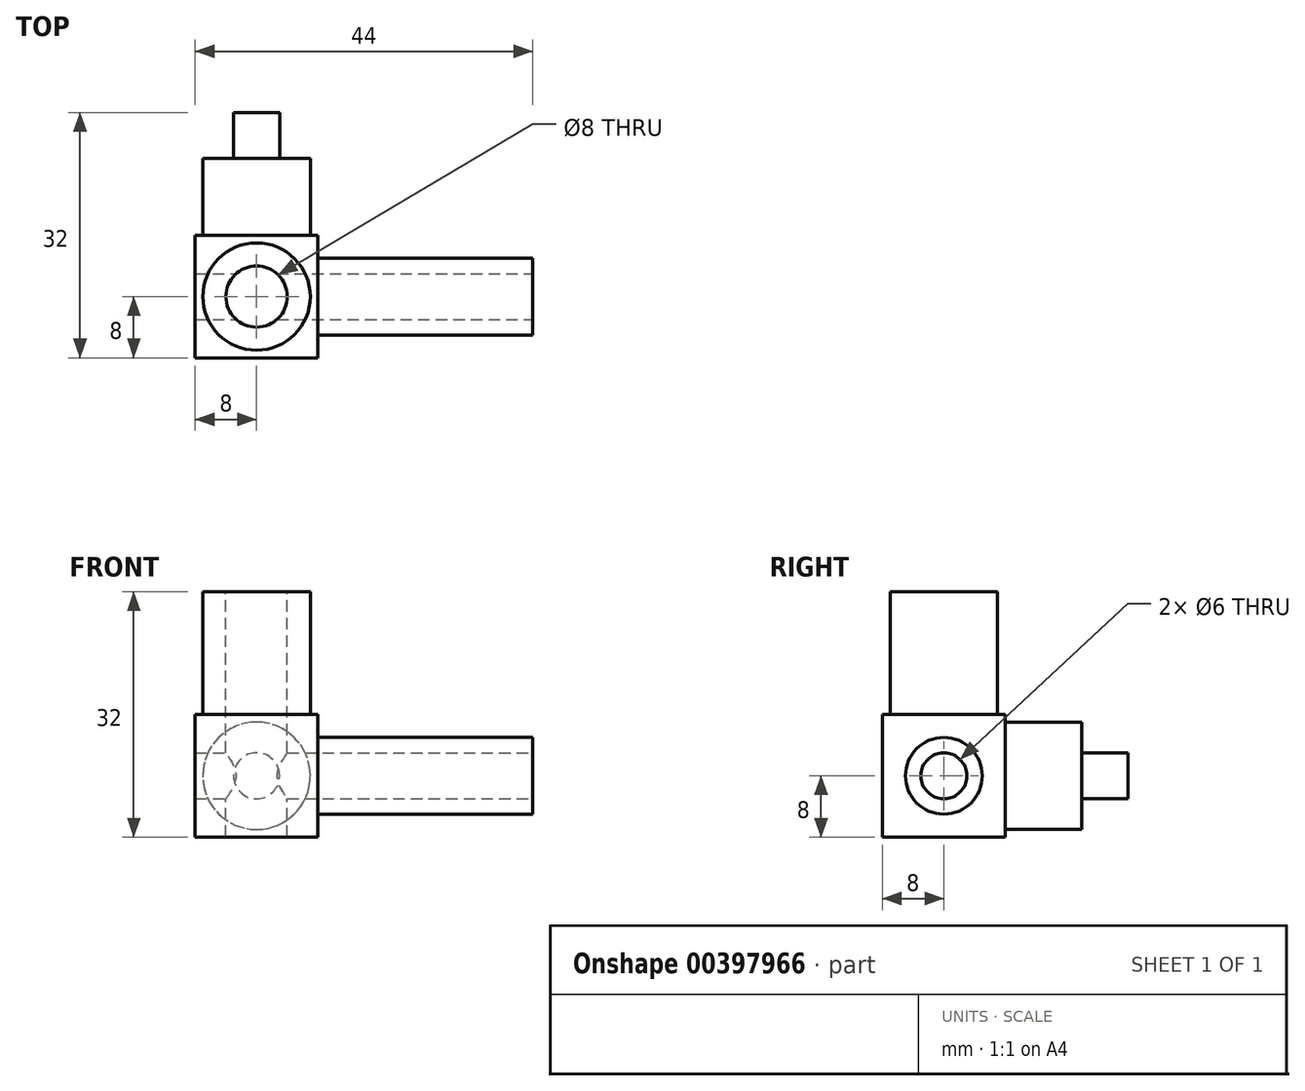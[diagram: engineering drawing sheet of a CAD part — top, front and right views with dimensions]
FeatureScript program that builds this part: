
annotation { "Feature Type Name" : "Feature", "Feature Type Description" : "" }
export const myFeature = defineFeature(function(context is Context, id is Id, definition is map)
    precondition{}
    {
        {
            var Q0;
            Q0=qCreatedBy(makeId("Right.planeOp"),FACE);
            var sketch = newSketch(context, id + "F0", { "sketchPlane" : qUnion([Q0])});
            skLineSegment(sketch, "E0.bottom", {"start": v(0, 0) * mm, "end": v(16, 0) * mm});
            skLineSegment(sketch, "E0.top", {"start": v(0, 16) * mm, "end": v(16, 16) * mm});
            skLineSegment(sketch, "E0.left", {"start": v(0, 0) * mm, "end": v(0, 16) * mm});
            skLineSegment(sketch, "E0.right", {"start": v(16, 0) * mm, "end": v(16, 16) * mm});
            skSolve(sketch);
        }
        {
            var Q0;
            Q0=makeQuery(id+"F0.imprint","IMPRINT",FACE,{"disambiguationData":[TD([[makeQuery(id+"F0.imprint","IMPRINT",EDGE,{"derivedFrom":sQuery(id+"F0.wireOp",EDGE,"E0.bottom")}),1.0]])]});
            extrude(context, id + "F1", {"entities" : qUnion([Q0]), "depth" : 16 * mm});
        }
        {
            var Q0;
            Q0=makeQuery(id+"F1.opExtrude","SWEPT_FACE",FACE,{"disambiguationData":[OSD([sQuery(id+"F0.wireOp",EDGE,"E0.top")])]});
            var sketch = newSketch(context, id + "F2", { "sketchPlane" : qUnion([Q0])});
            skLineSegment(sketch, "E1", {"start": v(8, -2.65) * mm, "end": v(8, 32.4) * mm, "construction": true});
            skLineSegment(sketch, "E2", {"start": v(-12.21, 8) * mm, "end": v(23.43, 8) * mm, "construction": true});
            skPoint(sketch, "E2.endSnap0", {"position": v(16, 8) * mm});
            skCircle(sketch, "E3", {"center": v(8, 8) * mm, "radius": 7 * mm});
            skSolve(sketch);
        }
        {
            var Q0;
            Q0=makeQuery(id+"F2.imprint","IMPRINT",FACE,{"disambiguationData":[TD([[makeQuery(id+"F2.imprint","IMPRINT",EDGE,{"derivedFrom":sQuery(id+"F2.wireOp",EDGE,"E3")}),1.0]])]});
            extrude(context, id + "F3", {"entities" : qUnion([Q0]), "operationType" : NewBodyOperationType.ADD, "depth" : 16 * mm});
        }
        {
            var Q0;
            Q0=makeQuery(id+"F3.opExtrude","CAP_FACE",FACE,{"disambiguationData":[OSD([sQuery(id+"F2.wireOp",EDGE,"E3")])],"isStart":false});
            var sketch = newSketch(context, id + "F4", { "sketchPlane" : qUnion([Q0])});
            skLineSegment(sketch, "E4", {"start": v(-6.93, 8) * mm, "end": v(26.94, 8) * mm, "construction": true});
            skLineSegment(sketch, "E5", {"start": v(8, 21.39) * mm, "end": v(8, -8.14) * mm, "construction": true});
            skCircle(sketch, "E6", {"center": v(8, 8) * mm, "radius": 4 * mm});
            skSolve(sketch);
        }
        {
            var Q0;
            Q0=makeQuery(id+"F4.imprint","IMPRINT",FACE,{"disambiguationData":[TD([[makeQuery(id+"F4.imprint","IMPRINT",EDGE,{"derivedFrom":sQuery(id+"F4.wireOp",EDGE,"E6")}),1.0]])]});
            var Q1;
            Q1=sQuery(id+"F4.wireOp",EDGE,"E5");
            var Q2;
            Q2=sQuery(id+"F4.wireOp",EDGE,"E4");
            extrude(context, id + "F5", {"entities" : qUnion([Q0]), "operationType" : NewBodyOperationType.REMOVE, "surfaceEntities" : qUnion([Q1, Q2]), "oppositeDirection" : true, "depth" : 34 * mm});
        }
        {
            var Q0;
            Q0=makeQuery(id+"F1.opExtrude","CAP_FACE",FACE,{"disambiguationData":[OSD([sQuery(id+"F0.wireOp",EDGE,"E0.bottom"),sQuery(id+"F0.wireOp",EDGE,"E0.top"),sQuery(id+"F0.wireOp",EDGE,"E0.left"),sQuery(id+"F0.wireOp",EDGE,"E0.right")])],"isStart":false});
            var sketch = newSketch(context, id + "F6", { "sketchPlane" : qUnion([Q0])});
            skLineSegment(sketch, "E7", {"start": v(30, 8) * mm, "end": v(-12.4, 8) * mm, "construction": true});
            skLineSegment(sketch, "E8", {"start": v(8, 26.22) * mm, "end": v(8, -7.63) * mm, "construction": true});
            skPoint(sketch, "E8.endSnap0", {"position": v(8, 0) * mm});
            skCircle(sketch, "E9", {"center": v(8, 8) * mm, "radius": 5 * mm});
            skCircle(sketch, "E10", {"center": v(8, 8) * mm, "radius": 3 * mm});
            skSolve(sketch);
        }
        {
            var Q0;
            Q0=makeQuery(id+"F6.imprint","IMPRINT",FACE,{"disambiguationData":[TD([[makeQuery(id+"F6.imprint","IMPRINT",EDGE,{"derivedFrom":sQuery(id+"F6.wireOp",EDGE,"E10")}),1.0]])]});
            extrude(context, id + "F7", {"entities" : qUnion([Q0]), "operationType" : NewBodyOperationType.REMOVE, "oppositeDirection" : true, "depth" : 18 * mm});
        }
        {
            var Q0;
            Q0=makeQuery(id+"F6.imprint","IMPRINT",FACE,{"disambiguationData":[TD([[makeQuery(id+"F6.imprint","IMPRINT",EDGE,{"derivedFrom":sQuery(id+"F6.wireOp",EDGE,"E9")}),1.0]])]});
            extrude(context, id + "F8", {"entities" : qUnion([Q0]), "operationType" : NewBodyOperationType.ADD, "depth" : 28 * mm});
        }
        {
            var Q0;
            Q0=makeQuery(id+"F1.opExtrude","SWEPT_FACE",FACE,{"disambiguationData":[OSD([sQuery(id+"F0.wireOp",EDGE,"E0.right")])]});
            var sketch = newSketch(context, id + "F9", { "sketchPlane" : qUnion([Q0])});
            skLineSegment(sketch, "E11", {"start": v(-22.61, 8) * mm, "end": v(7.95, 8) * mm, "construction": true});
            skLineSegment(sketch, "E12", {"start": v(-8, 19.36) * mm, "end": v(-8, -4.55) * mm, "construction": true});
            skCircle(sketch, "E13", {"center": v(-8, 8) * mm, "radius": 7 * mm});
            skCircle(sketch, "E14", {"center": v(-8, 8) * mm, "radius": 3 * mm});
            skSolve(sketch);
        }
        {
            var Q0;
            Q0=makeQuery(id+"F9.imprint","IMPRINT",FACE,{"disambiguationData":[TD([[makeQuery(id+"F9.imprint","IMPRINT",EDGE,{"derivedFrom":sQuery(id+"F9.wireOp",EDGE,"E14")}),1.0]])]});
            extrude(context, id + "F10", {"entities" : qUnion([Q0]), "operationType" : NewBodyOperationType.ADD, "depth" : 16 * mm});
        }
        {
            var Q0;
            Q0=makeQuery(id+"F9.imprint","IMPRINT",FACE,{"disambiguationData":[TD([[makeQuery(id+"F9.imprint","IMPRINT",EDGE,{"derivedFrom":sQuery(id+"F9.wireOp",EDGE,"E13")}),1.0]])]});
            extrude(context, id + "F11", {"entities" : qUnion([Q0]), "operationType" : NewBodyOperationType.ADD, "depth" : 10 * mm});
        }
    });
